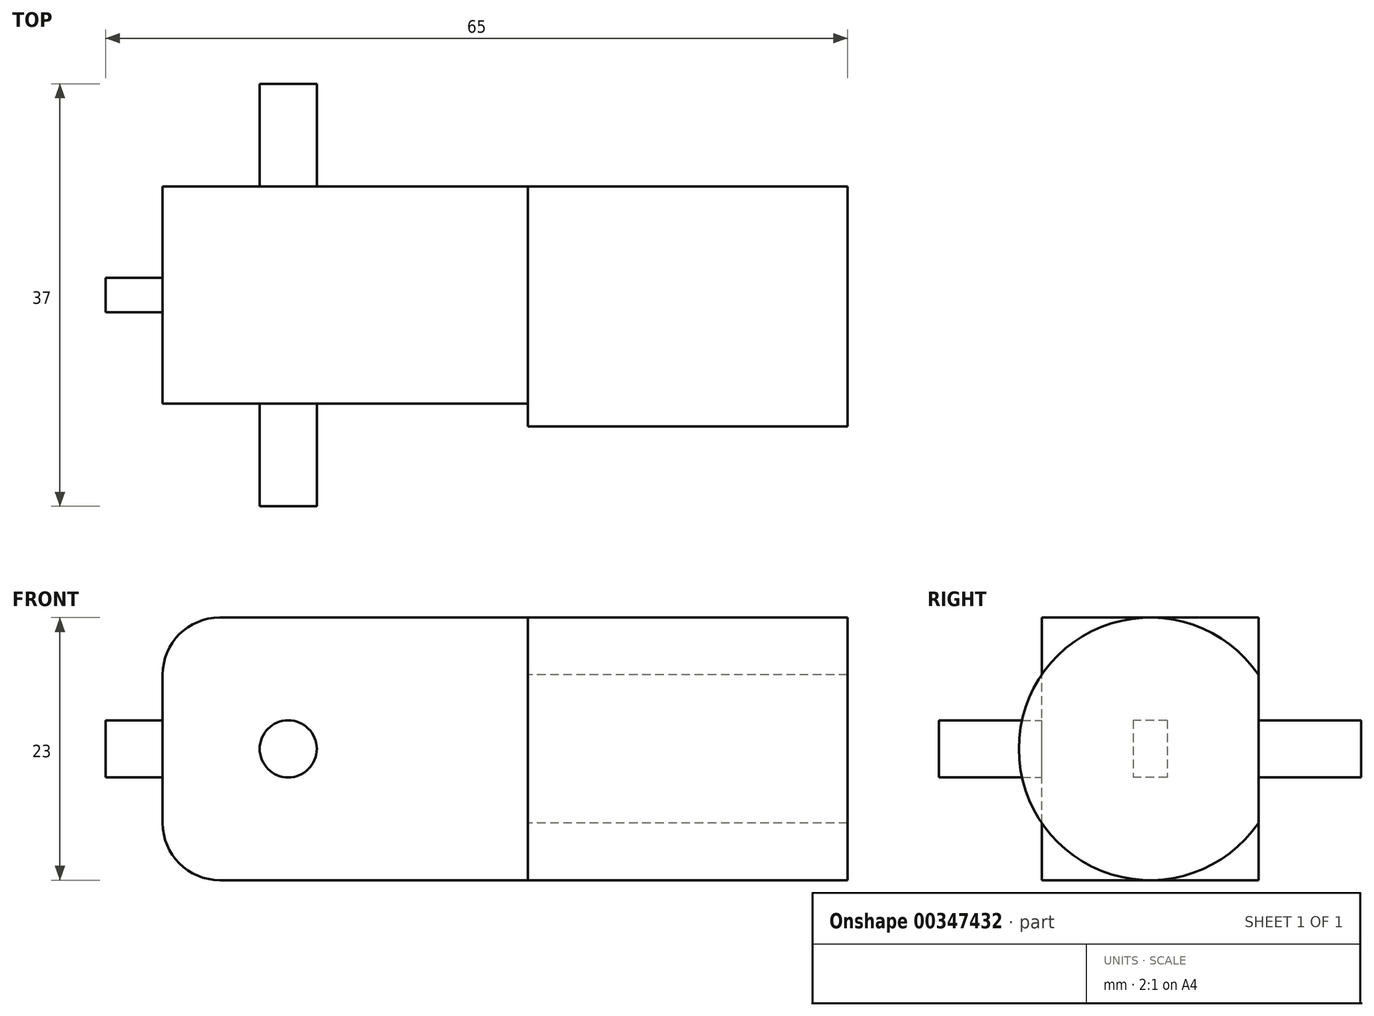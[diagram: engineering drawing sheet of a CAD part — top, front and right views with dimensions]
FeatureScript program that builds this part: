
annotation { "Feature Type Name" : "Feature", "Feature Type Description" : "" }
export const myFeature = defineFeature(function(context is Context, id is Id, definition is map)
    precondition{}
    {
        {
            var Q0;
            Q0=qCreatedBy(makeId("Front.planeOp"),FACE);
            var sketch = newSketch(context, id + "F0", { "sketchPlane" : qUnion([Q0])});
            skLineSegment(sketch, "E0.bottom", {"start": v(0, 0) * mm, "end": v(32, 0) * mm});
            skLineSegment(sketch, "E0.top", {"start": v(0, 23) * mm, "end": v(32, 23) * mm});
            skLineSegment(sketch, "E0.left", {"start": v(0, 0) * mm, "end": v(0, 23) * mm});
            skLineSegment(sketch, "E0.right", {"start": v(32, 0) * mm, "end": v(32, 23) * mm});
            skSolve(sketch);
        }
        {
            var Q0;
            Q0=makeQuery(id+"F0.imprint","IMPRINT",FACE,{"disambiguationData":[TD([[makeQuery(id+"F0.imprint","IMPRINT",EDGE,{"derivedFrom":sQuery(id+"F0.wireOp",EDGE,"E0.bottom")}),1.0]])]});
            extrude(context, id + "F1", {"entities" : qUnion([Q0]), "oppositeDirection" : true, "depth" : 19 * mm});
        }
        {
            var Q0;
            Q0=makeQuery(id+"F1.opExtrude","SWEPT_EDGE",EDGE,{"disambiguationData":[OSD([sQuery(id+"F0.wireOp",EDGE,"E0.top"),sQuery(id+"F0.wireOp",EDGE,"E0.left")])]});
            fillet(context, id + "F2", {"entities" : qUnion([Q0]), "radius" : 5 * mm, "tangentPropagation" : true, "allowEdgeOverflow" : false});
        }
        {
            var Q0;
            Q0=makeQuery(id+"F1.opExtrude","SWEPT_EDGE",EDGE,{"disambiguationData":[OSD([sQuery(id+"F0.wireOp",EDGE,"E0.bottom"),sQuery(id+"F0.wireOp",EDGE,"E0.left")])]});
            fillet(context, id + "F3", {"entities" : qUnion([Q0]), "radius" : 5 * mm, "tangentPropagation" : true, "allowEdgeOverflow" : false});
        }
        {
            var Q0;
            Q0=makeQuery(id+"F1.opExtrude","SWEPT_FACE",FACE,{"disambiguationData":[OSD([sQuery(id+"F0.wireOp",EDGE,"E0.left")])]});
            var sketch = newSketch(context, id + "F4", { "sketchPlane" : qUnion([Q0])});
            skLineSegment(sketch, "E1.bottom", {"start": v(-11, 14) * mm, "end": v(-8, 14) * mm});
            skLineSegment(sketch, "E1.top", {"start": v(-11, 9) * mm, "end": v(-8, 9) * mm});
            skLineSegment(sketch, "E1.left", {"start": v(-11, 14) * mm, "end": v(-11, 9) * mm});
            skLineSegment(sketch, "E1.right", {"start": v(-8, 14) * mm, "end": v(-8, 9) * mm});
            skSolve(sketch);
        }
        {
            var Q0;
            Q0=makeQuery(id+"F4.imprint","IMPRINT",FACE,{"disambiguationData":[TD([[makeQuery(id+"F4.imprint","IMPRINT",EDGE,{"derivedFrom":sQuery(id+"F4.wireOp",EDGE,"E1.bottom")}),-1.0]])]});
            extrude(context, id + "F5", {"entities" : qUnion([Q0]), "operationType" : NewBodyOperationType.ADD, "depth" : 5 * mm});
        }
        {
            var Q0;
            Q0=makeQuery(id+"F1.opExtrude","SWEPT_FACE",FACE,{"disambiguationData":[OSD([sQuery(id+"F0.wireOp",EDGE,"E0.right")])]});
            var sketch = newSketch(context, id + "F6", { "sketchPlane" : qUnion([Q0])});
            skCircle(sketch, "E2", {"center": v(9.5, 11.5) * mm, "radius": 11.5 * mm});
            skSolve(sketch);
        }
        {
            var Q0;
            {var subQ0=sQuery(id+"F6.wireOp",EDGE,"E2");var subQ1=makeQuery(id+"F1.opExtrude","CAP_EDGE",EDGE,{"disambiguationData":[OSD([sQuery(id+"F0.wireOp",EDGE,"E0.right")])],"isStart":true});var subQ2=makeQuery(id+"F6.imprint","INTERSECT",VERTEX,{"disambiguationData":[OD(0.0)],"derivedFrom":[subQ1,subQ0]});Q0=makeQuery(id+"F6.imprint","IMPRINT",FACE,{"disambiguationData":[TD([[makeQuery(id+"F6.imprint","IMPRINT",EDGE,{"disambiguationData":[TD([[subQ2,-1.0]])],"derivedFrom":subQ0}),1.0]])]});}
            var Q1;
            {var subQ0=sQuery(id+"F6.wireOp",EDGE,"E2");var subQ1=makeQuery(id+"F1.opExtrude","CAP_EDGE",EDGE,{"disambiguationData":[OSD([sQuery(id+"F0.wireOp",EDGE,"E0.right")])],"isStart":false});var subQ2=makeQuery(id+"F6.imprint","INTERSECT",VERTEX,{"disambiguationData":[OD(0.0)],"derivedFrom":[subQ1,subQ0]});Q1=makeQuery(id+"F6.imprint","IMPRINT",FACE,{"disambiguationData":[TD([[makeQuery(id+"F6.imprint","IMPRINT",EDGE,{"disambiguationData":[TD([[subQ2,1.0]])],"derivedFrom":subQ0}),1.0]])]});}
            var Q2;
            {var subQ0=sQuery(id+"F6.wireOp",EDGE,"E2");var subQ1=sQuery(id+"F0.wireOp",EDGE,"E0.right");var subQ2=makeQuery(id+"F1.opExtrude","CAP_EDGE",EDGE,{"disambiguationData":[OSD([subQ1])],"isStart":true});var subQ3=makeQuery(id+"F6.imprint","INTERSECT",VERTEX,{"disambiguationData":[OD(0.0)],"derivedFrom":[subQ2,subQ0]});Q2=makeQuery(id+"F6.imprint","IMPRINT",FACE,{"disambiguationData":[TD([[makeQuery(id+"F6.imprint","IMPRINT",EDGE,{"disambiguationData":[TD([[subQ3,1.0]])],"derivedFrom":subQ0}),1.0]])]});}
            extrude(context, id + "F7", {"entities" : qUnion([Q0, Q1, Q2]), "operationType" : NewBodyOperationType.ADD, "depth" : 28 * mm});
        }
        {
            var Q0;
            Q0=makeQuery(id+"F1.opExtrude","CAP_FACE",FACE,{"disambiguationData":[OSD([sQuery(id+"F0.wireOp",EDGE,"E0.bottom"),sQuery(id+"F0.wireOp",EDGE,"E0.top"),sQuery(id+"F0.wireOp",EDGE,"E0.left"),sQuery(id+"F0.wireOp",EDGE,"E0.right")])],"isStart":true});
            var sketch = newSketch(context, id + "F8", { "sketchPlane" : qUnion([Q0])});
            skCircle(sketch, "E3", {"center": v(11, 11.5) * mm, "radius": 2.5 * mm});
            skSolve(sketch);
        }
        {
            var Q0;
            Q0=makeQuery(id+"F8.imprint","IMPRINT",FACE,{"disambiguationData":[TD([[makeQuery(id+"F8.imprint","IMPRINT",EDGE,{"derivedFrom":sQuery(id+"F8.wireOp",EDGE,"E3")}),1.0]])]});
            extrude(context, id + "F9", {"entities" : qUnion([Q0]), "operationType" : NewBodyOperationType.ADD, "depth" : 9 * mm});
        }
        {
            var Q0;
            Q0=makeQuery(id+"F1.opExtrude","CAP_FACE",FACE,{"disambiguationData":[OSD([sQuery(id+"F0.wireOp",EDGE,"E0.bottom"),sQuery(id+"F0.wireOp",EDGE,"E0.top"),sQuery(id+"F0.wireOp",EDGE,"E0.left"),sQuery(id+"F0.wireOp",EDGE,"E0.right")])],"isStart":false});
            var sketch = newSketch(context, id + "F10", { "sketchPlane" : qUnion([Q0])});
            skCircle(sketch, "E4", {"center": v(-11, 11.5) * mm, "radius": 2.5 * mm});
            skSolve(sketch);
        }
        {
            var Q0;
            Q0=makeQuery(id+"F10.imprint","IMPRINT",FACE,{"disambiguationData":[TD([[makeQuery(id+"F10.imprint","IMPRINT",EDGE,{"derivedFrom":sQuery(id+"F10.wireOp",EDGE,"E4")}),1.0]])]});
            extrude(context, id + "F11", {"entities" : qUnion([Q0]), "operationType" : NewBodyOperationType.ADD, "depth" : 9 * mm});
        }
    });
